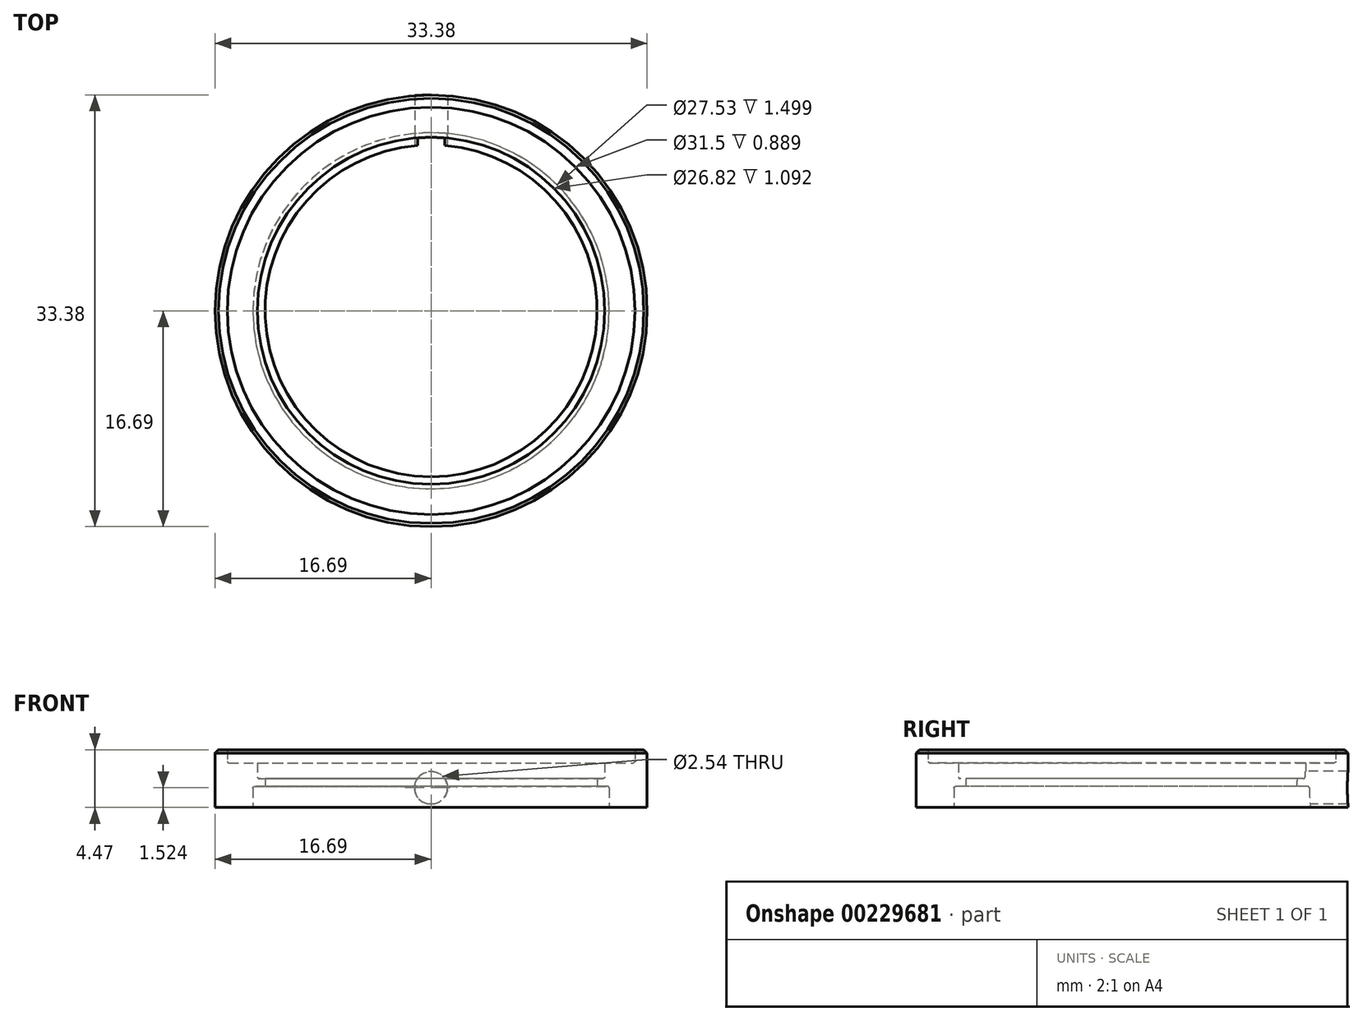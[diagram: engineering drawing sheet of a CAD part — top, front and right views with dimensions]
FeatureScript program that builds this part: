
annotation { "Feature Type Name" : "Feature", "Feature Type Description" : "" }
export const myFeature = defineFeature(function(context is Context, id is Id, definition is map)
    precondition{}
    {
        {
            var Q0;
            Q0=qCreatedBy(makeId("Front.planeOp"),FACE);
            var sketch = newSketch(context, id + "F0", { "sketchPlane" : qUnion([Q0])});
            skLineSegment(sketch, "E0", {"start": v(16.69, 4.22) * mm, "end": v(16.69, 0) * mm});
            skLineSegment(sketch, "E1", {"start": v(16.69, 0) * mm, "end": v(13.77, 0) * mm});
            skLineSegment(sketch, "E2", {"start": v(13.77, 0) * mm, "end": v(13.77, 1.5) * mm});
            skLineSegment(sketch, "E3", {"start": v(13.64, 1.63) * mm, "end": v(12.83, 1.63) * mm});
            skLineSegment(sketch, "E4", {"start": v(12.83, 1.63) * mm, "end": v(12.83, 2.24) * mm});
            skLineSegment(sketch, "E5", {"start": v(12.83, 2.24) * mm, "end": v(13.28, 2.24) * mm});
            skLineSegment(sketch, "E6", {"start": v(15.75, 3.58) * mm, "end": v(15.75, 4.47) * mm});
            skLineSegment(sketch, "E7", {"start": v(15.75, 4.47) * mm, "end": v(16.43, 4.47) * mm});
            skLineSegment(sketch, "E8", {"start": v(13.41, 2.36) * mm, "end": v(13.41, 3.45) * mm});
            skLineSegment(sketch, "E9", {"start": v(13.41, 3.45) * mm, "end": v(15.62, 3.45) * mm});
            skLineSegment(sketch, "E10", {"start": v(0, 0) * mm, "end": v(0, 6.21) * mm, "construction": true});
            skArc(sketch, "E11.filletArc", {"start": v(15.62, 3.45) * mm, "mid": v(15.71, 3.5) * mm, "end": v(15.75, 3.58) * mm});
            skArc(sketch, "E12.filletArc", {"start": v(13.28, 2.24) * mm, "mid": v(13.37, 2.27) * mm, "end": v(13.41, 2.36) * mm});
            skArc(sketch, "E13.filletArc", {"start": v(13.77, 1.5) * mm, "mid": v(13.73, 1.59) * mm, "end": v(13.64, 1.63) * mm});
            skLineSegment(sketch, "E14", {"start": v(16.69, 4.22) * mm, "end": v(16.43, 4.47) * mm});
            skSolve(sketch);
        }
        {
            var Q0;
            Q0=makeQuery(id+"F0.imprint","IMPRINT",FACE,{"disambiguationData":[TD([[makeQuery(id+"F0.imprint","IMPRINT",EDGE,{"derivedFrom":sQuery(id+"F0.wireOp",EDGE,"E0")}),-1.0]])]});
            var Q1;
            Q1=sQuery(id+"F0.wireOp",EDGE,"E10");
            var Q2;
            Q2=sQuery(id+"F0.wireOp",EDGE,"E10");
            revolve(context, id + "F1", {"entities" : qUnion([Q0]), "surfaceEntities" : qUnion([Q1]), "axis" : qUnion([Q2]), "revolveType" : RevolveType.FULL});
        }
        {
            var Q0;
            Q0=qCreatedBy(makeId("Front.planeOp"),FACE);
            var sketch = newSketch(context, id + "F2", { "sketchPlane" : qUnion([Q0])});
            skCircle(sketch, "E15", {"center": v(0, 1.52) * mm, "radius": 1.27 * mm});
            skSolve(sketch);
        }
        {
            var Q0;
            Q0=makeQuery(id+"F2.imprint","IMPRINT",FACE,{"disambiguationData":[TD([[makeQuery(id+"F2.imprint","IMPRINT",EDGE,{"derivedFrom":sQuery(id+"F2.wireOp",EDGE,"E15")}),1.0]])]});
            extrude(context, id + "F3", {"entities" : qUnion([Q0]), "operationType" : NewBodyOperationType.REMOVE, "oppositeDirection" : true, "depth" : 25.4 * mm});
        }
    });
